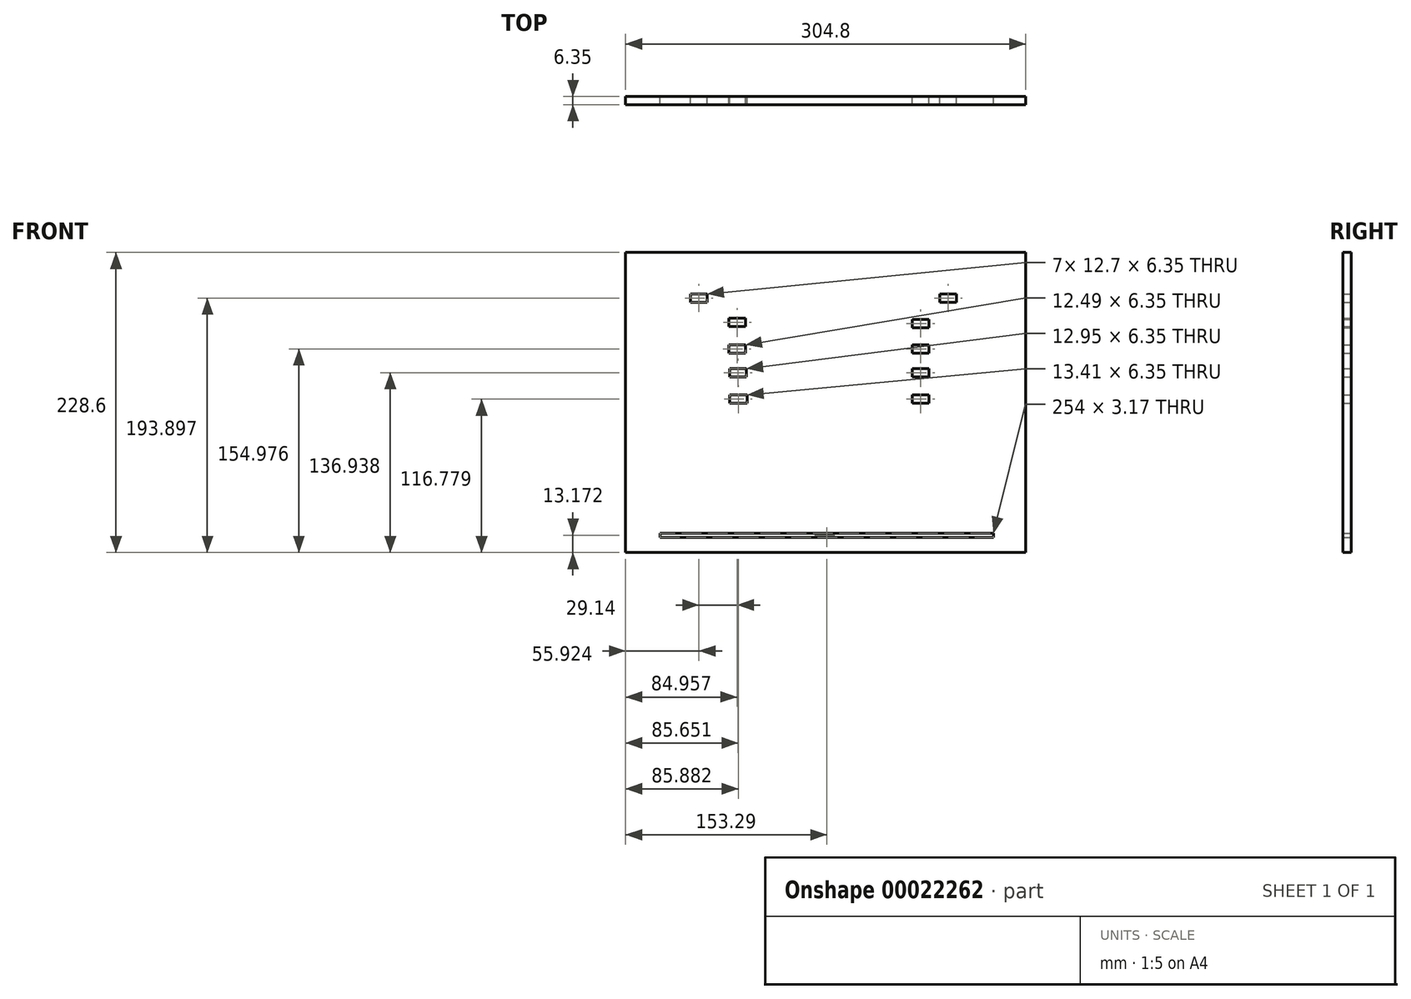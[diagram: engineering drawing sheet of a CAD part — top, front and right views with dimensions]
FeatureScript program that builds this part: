
annotation { "Feature Type Name" : "Feature", "Feature Type Description" : "" }
export const myFeature = defineFeature(function(context is Context, id is Id, definition is map)
    precondition{}
    {
        {
            var Q0;
            Q0=qCreatedBy(makeId("Front.planeOp"),FACE);
            var sketch = newSketch(context, id + "F0", { "sketchPlane" : qUnion([Q0])});
            skLineSegment(sketch, "E0.bottom", {"start": v(-148.7, 95.18) * mm, "end": v(156.1, 95.18) * mm});
            skLineSegment(sketch, "E0.top", {"start": v(-148.7, -133.42) * mm, "end": v(156.1, -133.42) * mm});
            skLineSegment(sketch, "E0.left", {"start": v(-148.7, 95.18) * mm, "end": v(-148.7, -133.42) * mm});
            skLineSegment(sketch, "E0.right", {"start": v(156.1, 95.18) * mm, "end": v(156.1, -133.42) * mm});
            skLineSegment(sketch, "E1.bottom", {"start": v(74.01, 95.47) * mm, "end": v(134, 95.47) * mm, "construction": true});
            skLineSegment(sketch, "E2.bottom", {"start": v(-69.98, 45.15) * mm, "end": v(-57.28, 45.15) * mm});
            skLineSegment(sketch, "E2.top", {"start": v(-69.98, 38.8) * mm, "end": v(-57.28, 38.8) * mm});
            skLineSegment(sketch, "E2.left", {"start": v(-69.98, 45.15) * mm, "end": v(-69.98, 38.8) * mm});
            skLineSegment(sketch, "E2.right", {"start": v(-57.28, 45.15) * mm, "end": v(-57.28, 38.8) * mm});
            skLineSegment(sketch, "E3.bottom", {"start": v(69.68, 44.17) * mm, "end": v(82.38, 44.17) * mm});
            skLineSegment(sketch, "E3.top", {"start": v(69.68, 37.82) * mm, "end": v(82.38, 37.82) * mm});
            skLineSegment(sketch, "E3.left", {"start": v(69.68, 44.17) * mm, "end": v(69.68, 37.82) * mm});
            skLineSegment(sketch, "E3.right", {"start": v(82.38, 44.17) * mm, "end": v(82.38, 37.82) * mm});
            skLineSegment(sketch, "E4.bottom", {"start": v(-69.98, 24.73) * mm, "end": v(-57.49, 24.73) * mm});
            skLineSegment(sketch, "E4.top", {"start": v(-69.98, 18.38) * mm, "end": v(-57.49, 18.38) * mm});
            skLineSegment(sketch, "E4.left", {"start": v(-69.98, 24.73) * mm, "end": v(-69.98, 18.38) * mm});
            skLineSegment(sketch, "E4.right", {"start": v(-57.49, 24.73) * mm, "end": v(-57.49, 18.38) * mm});
            skLineSegment(sketch, "E5.bottom", {"start": v(69.68, 24.73) * mm, "end": v(82.38, 24.73) * mm});
            skLineSegment(sketch, "E5.top", {"start": v(69.68, 18.38) * mm, "end": v(82.38, 18.38) * mm});
            skLineSegment(sketch, "E5.left", {"start": v(69.68, 24.73) * mm, "end": v(69.68, 18.38) * mm});
            skLineSegment(sketch, "E5.right", {"start": v(82.38, 24.73) * mm, "end": v(82.38, 18.38) * mm});
            skLineSegment(sketch, "E6.bottom", {"start": v(-69.51, 6.7) * mm, "end": v(-56.56, 6.7) * mm});
            skLineSegment(sketch, "E6.top", {"start": v(-69.51, 0.34) * mm, "end": v(-56.56, 0.34) * mm});
            skLineSegment(sketch, "E6.left", {"start": v(-69.51, 6.7) * mm, "end": v(-69.51, 0.34) * mm});
            skLineSegment(sketch, "E6.right", {"start": v(-56.56, 6.7) * mm, "end": v(-56.56, 0.34) * mm});
            skLineSegment(sketch, "E7.bottom", {"start": v(69.68, 6.7) * mm, "end": v(82.38, 6.7) * mm});
            skLineSegment(sketch, "E7.top", {"start": v(69.68, 0.34) * mm, "end": v(82.38, 0.34) * mm});
            skLineSegment(sketch, "E7.left", {"start": v(69.68, 6.7) * mm, "end": v(69.68, 0.34) * mm});
            skLineSegment(sketch, "E7.right", {"start": v(82.38, 6.7) * mm, "end": v(82.38, 0.34) * mm});
            skLineSegment(sketch, "E8.bottom", {"start": v(-69.51, -13.47) * mm, "end": v(-56.1, -13.47) * mm});
            skLineSegment(sketch, "E8.top", {"start": v(-69.51, -19.82) * mm, "end": v(-56.1, -19.82) * mm});
            skLineSegment(sketch, "E8.left", {"start": v(-69.51, -13.47) * mm, "end": v(-69.51, -19.82) * mm});
            skLineSegment(sketch, "E8.right", {"start": v(-56.1, -13.47) * mm, "end": v(-56.1, -19.82) * mm});
            skLineSegment(sketch, "E9.bottom", {"start": v(69.68, -13.47) * mm, "end": v(82.38, -13.47) * mm});
            skLineSegment(sketch, "E9.top", {"start": v(69.68, -19.82) * mm, "end": v(82.38, -19.82) * mm});
            skLineSegment(sketch, "E9.left", {"start": v(69.68, -13.47) * mm, "end": v(69.68, -19.82) * mm});
            skLineSegment(sketch, "E9.right", {"start": v(82.38, -13.47) * mm, "end": v(82.38, -19.82) * mm});
            skLineSegment(sketch, "E10.bottom", {"start": v(-99.12, 63.65) * mm, "end": v(-86.42, 63.65) * mm});
            skLineSegment(sketch, "E10.top", {"start": v(-99.12, 57.3) * mm, "end": v(-86.42, 57.3) * mm});
            skLineSegment(sketch, "E10.left", {"start": v(-99.12, 63.65) * mm, "end": v(-99.12, 57.3) * mm});
            skLineSegment(sketch, "E10.right", {"start": v(-86.42, 63.65) * mm, "end": v(-86.42, 57.3) * mm});
            skLineSegment(sketch, "E11.bottom", {"start": v(103.44, 63.65) * mm, "end": v(90.74, 63.65) * mm});
            skLineSegment(sketch, "E11.top", {"start": v(103.44, 57.3) * mm, "end": v(90.74, 57.3) * mm});
            skLineSegment(sketch, "E11.left", {"start": v(103.44, 63.65) * mm, "end": v(103.44, 57.3) * mm});
            skLineSegment(sketch, "E11.right", {"start": v(90.74, 63.65) * mm, "end": v(90.74, 57.3) * mm});
            skLineSegment(sketch, "E12", {"start": v(-148.7, 95.18) * mm, "end": v(-72.5, 95.18) * mm});
            skLineSegment(sketch, "E13", {"start": v(156.1, 95.18) * mm, "end": v(156.1, 95.18) * mm});
            skLineSegment(sketch, "E14.bottom", {"start": v(-122.4, -118.66) * mm, "end": v(131.6, -118.66) * mm});
            skLineSegment(sketch, "E14.top", {"start": v(-122.4, -121.84) * mm, "end": v(131.6, -121.84) * mm});
            skLineSegment(sketch, "E14.left", {"start": v(-122.4, -118.66) * mm, "end": v(-122.4, -121.84) * mm});
            skLineSegment(sketch, "E14.right", {"start": v(131.6, -118.66) * mm, "end": v(131.6, -121.84) * mm});
            skSolve(sketch);
        }
        {
            var Q0;
            Q0=makeQuery(id+"F0.imprint","IMPRINT",FACE,{"disambiguationData":[TD([[makeQuery(id+"F0.imprint","IMPRINT",EDGE,{"derivedFrom":sQuery(id+"F0.wireOp",EDGE,"E0.bottom")}),-1.0]])]});
            extrude(context, id + "F1", {"entities" : qUnion([Q0]), "depth" : 6.35 * mm});
        }
    });
